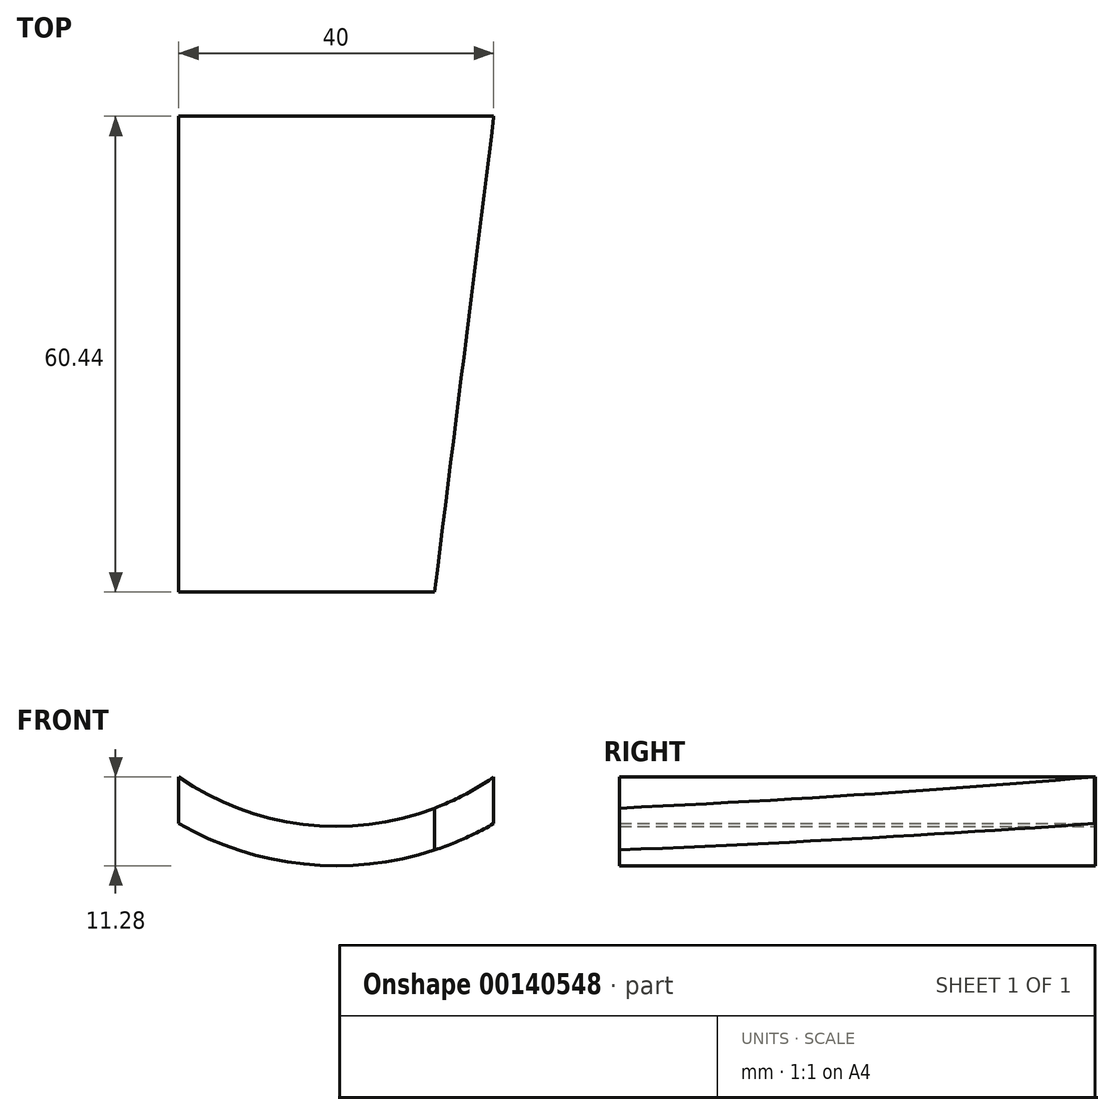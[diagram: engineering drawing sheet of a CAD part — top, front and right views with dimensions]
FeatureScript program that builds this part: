
annotation { "Feature Type Name" : "Feature", "Feature Type Description" : "" }
export const myFeature = defineFeature(function(context is Context, id is Id, definition is map)
    precondition{}
    {
        {
            var Q0;
            Q0=qCreatedBy(makeId("Top.planeOp"),FACE);
            var sketch = newSketch(context, id + "F0", { "sketchPlane" : qUnion([Q0])});
            skLineSegment(sketch, "E0", {"start": v(-12.5, 0) * mm, "end": v(12.5, 0) * mm});
            skLineSegment(sketch, "E1", {"start": v(12.5, 0) * mm, "end": v(20, 60.28) * mm});
            skLineSegment(sketch, "E2", {"start": v(-20, 60.28) * mm, "end": v(-12.5, 0) * mm});
            skLineSegment(sketch, "E3", {"start": v(-20, 60.28) * mm, "end": v(20, 60.28) * mm});
            skSolve(sketch);
        }
        {
            var Q0;
            Q0=qCreatedBy(makeId("Top.planeOp"),FACE);
            var sketch = newSketch(context, id + "F1", { "sketchPlane" : qUnion([Q0])});
            skLineSegment(sketch, "E4", {"start": v(0, 0) * mm, "end": v(0, 60.44) * mm});
            skSolve(sketch);
        }
        {
            var Q0;
            Q0=sQuery(id+"F0.wireOp",EDGE,"E3");
            cPlane(context, id + "F2", {"entities" : qUnion([Q0]), "cplaneType" : CPlaneType.LINE_ANGLE, "offset" : 25 * mm, "angle" : 0 * degree, "width" : 150 * mm, "height" : 150 * mm});
        }
        {
            var Q0;
            Q0=qCreatedBy(id+"F2.planeOp",FACE);
            var sketch = newSketch(context, id + "F3", { "sketchPlane" : qUnion([Q0])});
            skLineSegment(sketch, "E5", {"start": v(0, 0) * mm, "end": v(0, 5) * mm, "construction": true});
            skLineSegment(sketch, "E6", {"start": v(20, 5.36) * mm, "end": v(20, 11.28) * mm});
            skLineSegment(sketch, "E7.MirrorCS", {"start": v(-20, 5.36) * mm, "end": v(-20, 11.28) * mm});
            skArc(sketch, "E8", {"start": v(-20, 5.36) * mm, "mid": v(0, 0) * mm, "end": v(20, 5.36) * mm});
            skPoint(sketch, "E9.orphan", {"position": v(-20, 0) * mm});
            skPoint(sketch, "E10.start.orphan", {"position": v(20, 0) * mm});
            skArc(sketch, "E11.0", {"start": v(-20, 11.28) * mm, "mid": v(0, 5) * mm, "end": v(20, 11.28) * mm});
            skPoint(sketch, "E12.orphan", {"position": v(0, 0) * mm});
            skSolve(sketch);
        }
        {
            var Q0;
            Q0=makeQuery(id+"F3.imprint","IMPRINT",FACE,{"disambiguationData":[TD([[makeQuery(id+"F3.imprint","IMPRINT",EDGE,{"derivedFrom":sQuery(id+"F3.wireOp",EDGE,"E6")}),1.0]])]});
            var Q1;
            Q1=sQuery(id+"F1.wireOp",EDGE,"E4");
            sweep(context, id + "F4", {"profiles" : qUnion([Q0]), "path" : qUnion([Q1])});
        }
        {
            var Q0;
            Q0=sQuery(id+"F0.wireOp",EDGE,"E1");
            cPlane(context, id + "F5", {"entities" : qUnion([Q0]), "cplaneType" : CPlaneType.LINE_ANGLE, "offset" : 25 * mm, "angle" : 90 * degree, "width" : 150 * mm, "height" : 150 * mm});
        }
        {
            var Q0;
            Q0=makeQuery(id+"F4.opSweep","SWEPT_FACE",FACE,{"disambiguationData":[OSD([sQuery(id+"F1.wireOp",EDGE,"E4"),sQuery(id+"F3.wireOp",EDGE,"E7.MirrorCS")])]});
            var Q1;
            Q1=qCreatedBy(id+"F5.planeOp",FACE);
            extrude(context, id + "F6", {"entities" : qUnion([Q0]), "operationType" : NewBodyOperationType.REMOVE, "endBound" : BoundingType.UP_TO_SURFACE, "oppositeDirection" : true, "endBoundEntityFace" : qUnion([Q1]), "depth" : 25 * mm, "hasDraft" : true, "draftAngle" : 30 * degree});
        }
    });
